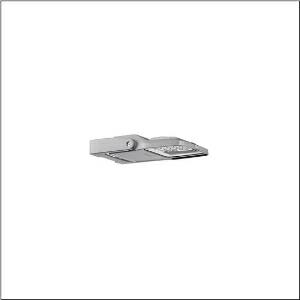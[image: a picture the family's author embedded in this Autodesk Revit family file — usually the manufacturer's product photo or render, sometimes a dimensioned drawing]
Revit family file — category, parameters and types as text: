
# Revit family: floodlight_fl_21_micro___pl61_5xa7761a4c2a_ae88
name_source: partatom
category: Lighting Fixtures
units: mm (PartAtom-declared; Revit-internal decimal feet)

## family parameters
Cut with Voids When Loaded = No
Host = Face
Light Source = No
Part Type = Normal
Room Calculation Point = No
Round Connector Dimension = Use Diameter
Shared = No

## types (1)
- --- (1 x LED, 3030 lm, 23.1 W, 4000K)
    Apparent Load = 23 VA
    CIE Flux Codes = 33 65 98 100 100
    Color Rendering = 70
    Color Temperature = 4000K
    Default Elevation = 1800 mm
    Description = Floodlight FL 21 micro, floodlight, primary light control with lens, of PMMA, primary optical cover: protective disc, of toughened safety glass, transparent, light distribution: PL61, light emission: direct distribution, installation type: surface-mounted, LED, High Power LED, rated luminous flux: 3.030lm, luminous efficacy: 131lm/W, light colour: 740, colour temperature: 4000K, control gear: ECG iQ, control: optimised constant luminous flux control (CLO 2.0), Desk-Remote (wireless, voltage-free reading and setting of iQ features in the workshop via application-optimized NFC function/RFID function), Light-Fading, Smart-Wire, Night-Set, Lumen-Switch, Temp-Guard, Auto-Match, with terminal, 6-pole, mains connection: 220..240V, AC, 50/60Hz, start of lifetime: 23W, end of lifetime: 24W, reduction: 11W, luminaire housing, of diecast aluminium, powder-coated, Siteco® metallic grey (DB 702S), corrosivity category C5 according to DIN EN ISO 12944, design bracket, of diecast aluminium, powder-coated, Siteco® metallic grey (DB 702S), protection rating (complete): IP66, insulation class (complete): insulation class II (safety insulation), certification: CE, protection symbol: D, impact resistance: IK07, permissible operating ambient temperature: -40..+40°C, permissible operating ambient temperature for outdoor applications: -40..+50°C, standard: DIN EN 12944, packaging unit: 1 piece

Light Distribution: PL61
    Height = 65 mm
    Lamp = 1 x LED
    Lamp Light Flux = 3030 lm
    Lamp Power = 23.1 W
    Lamp count = 1
    Length = 312 mm
    Luminous efficacy = 131 lm/W
    Manufacturer = Siteco
    ModVariant = No
    Model = 5XA7761A4C2A
    Number of Poles = 1
    OnlyDefault = Yes
    Power Factor = 1
    Product Name = Floodlight FL 21 micro | PL61
    Product group = floodlight | pylon top
    ProductGroupID = 6101
    Protection Class = Protection class II
    Protection Degree = IP 66
    RLX_Detail_Level = 1
    RlxData = <blob elided: 97461 chars, md5=7c294184>
    Socket = socket
    Standby Power = 0 W
    System Light Flux = 3030 lm
    System Power = 23 W
    Type Comments = factory setting: luminous flux: 100 % | dim-lin: 254 | 455 mA
    Type Image = l_1006878.jpg
    URL = http://relux.com
    VarID = @adj_115471
    Voltage = 0 V
    Weight = 0.00 kg
    Width = 230 mm

## geometry (parser evidence)
native form markers: Blend x4, Sweep x12
no freeform markers — native parametric forms only
